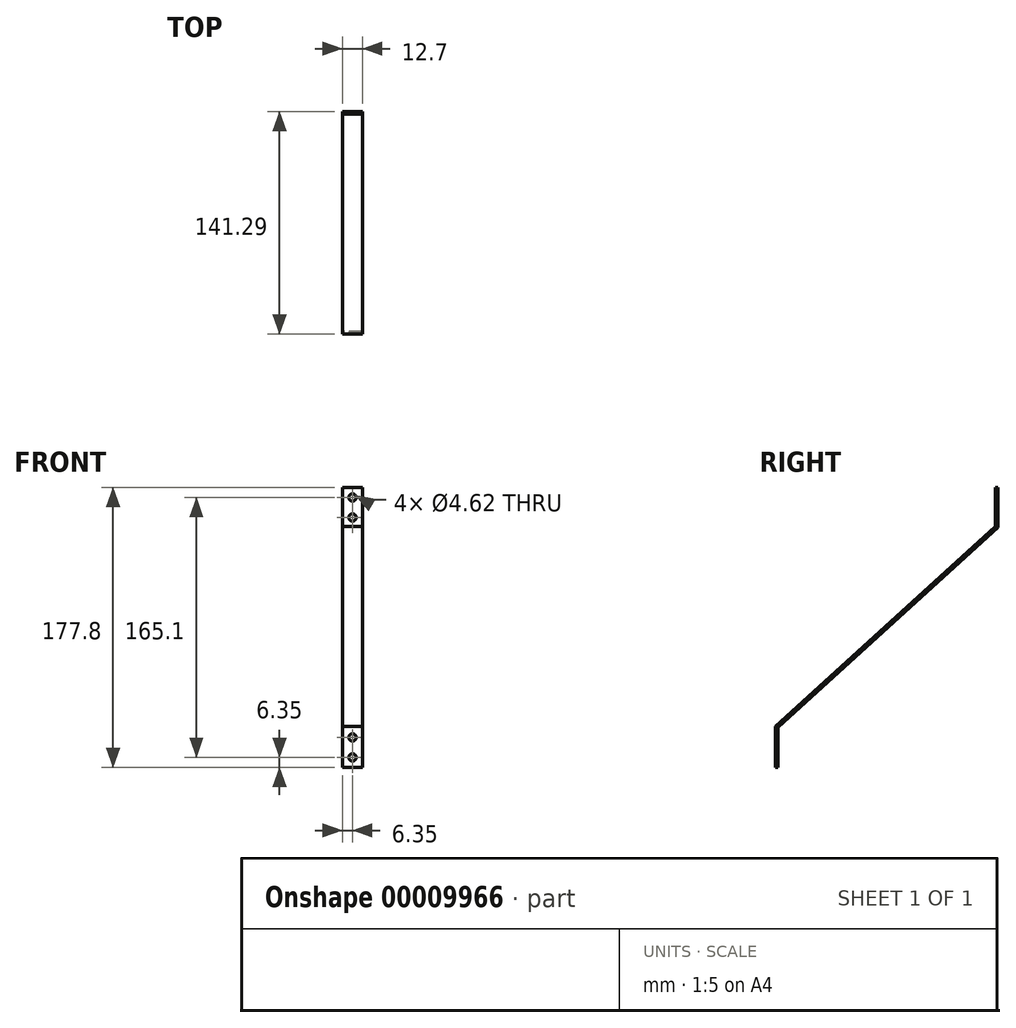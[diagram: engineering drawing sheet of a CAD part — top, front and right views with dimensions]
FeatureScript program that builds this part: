
annotation { "Feature Type Name" : "Feature", "Feature Type Description" : "" }
export const myFeature = defineFeature(function(context is Context, id is Id, definition is map)
    precondition{}
    {
        {
            var Q0;
            Q0=qCreatedBy(makeId("Right.planeOp"),FACE);
            var sketch = newSketch(context, id + "F0", { "sketchPlane" : qUnion([Q0])});
            skLineSegment(sketch, "E0", {"start": v(0, 0) * mm, "end": v(0, 25.4) * mm});
            skLineSegment(sketch, "E1", {"start": v(139.7, 152.4) * mm, "end": v(0, 25.4) * mm});
            skLineSegment(sketch, "E2", {"start": v(139.7, 152.4) * mm, "end": v(139.7, 177.8) * mm});
            skLineSegment(sketch, "E3", {"start": v(139.7, 177.8) * mm, "end": v(138.11, 177.8) * mm});
            skLineSegment(sketch, "E4", {"start": v(138.11, 177.8) * mm, "end": v(138.11, 153.1) * mm});
            skLineSegment(sketch, "E5", {"start": v(-1.59, 26.1) * mm, "end": v(138.11, 153.1) * mm});
            skLineSegment(sketch, "E6", {"start": v(-1.59, 26.1) * mm, "end": v(-1.59, 0) * mm});
            skLineSegment(sketch, "E7", {"start": v(-1.59, 0) * mm, "end": v(0, 0) * mm});
            skSolve(sketch);
        }
        {
            var Q0;
            Q0=makeQuery(id+"F0.imprint","IMPRINT",FACE,{"disambiguationData":[TD([[makeQuery(id+"F0.imprint","IMPRINT",EDGE,{"derivedFrom":sQuery(id+"F0.wireOp",EDGE,"E0")}),1.0]])]});
            extrude(context, id + "F1", {"entities" : qUnion([Q0]), "depth" : 12.7 * mm});
        }
        {
            var Q0;
            Q0=makeQuery(id+"F1.opExtrude","SWEPT_FACE",FACE,{"disambiguationData":[OSD([sQuery(id+"F0.wireOp",EDGE,"E4")])]});
            var sketch = newSketch(context, id + "F2", { "sketchPlane" : qUnion([Q0])});
            skCircle(sketch, "E8", {"center": v(6.35, 171.45) * mm, "radius": 2.31 * mm});
            skCircle(sketch, "E9", {"center": v(6.35, 158.75) * mm, "radius": 2.31 * mm});
            skPoint(sketch, "E10", {"position": v(6.35, 177.8) * mm});
            skSolve(sketch);
        }
        {
            var Q0;
            Q0=makeQuery(id+"F2.imprint","IMPRINT",FACE,{"disambiguationData":[TD([[makeQuery(id+"F2.imprint","IMPRINT",EDGE,{"derivedFrom":sQuery(id+"F2.wireOp",EDGE,"E8")}),1.0]])]});
            var Q1;
            Q1=makeQuery(id+"F2.imprint","IMPRINT",FACE,{"disambiguationData":[TD([[makeQuery(id+"F2.imprint","IMPRINT",EDGE,{"derivedFrom":sQuery(id+"F2.wireOp",EDGE,"E9")}),1.0]])]});
            extrude(context, id + "F3", {"entities" : qUnion([Q0, Q1]), "operationType" : NewBodyOperationType.REMOVE, "endBound" : BoundingType.THROUGH_ALL, "oppositeDirection" : true, "depth" : 25.4 * mm});
        }
        {
            var Q0;
            Q0=makeQuery(id+"F1.opExtrude","SWEPT_FACE",FACE,{"disambiguationData":[OSD([sQuery(id+"F0.wireOp",EDGE,"E6")])]});
            var sketch = newSketch(context, id + "F4", { "sketchPlane" : qUnion([Q0])});
            skCircle(sketch, "E11", {"center": v(6.35, 6.35) * mm, "radius": 2.31 * mm});
            skCircle(sketch, "E12", {"center": v(6.35, 19.05) * mm, "radius": 2.31 * mm});
            skPoint(sketch, "E13", {"position": v(6.35, 0) * mm});
            skSolve(sketch);
        }
        {
            var Q0;
            Q0=makeQuery(id+"F4.imprint","IMPRINT",FACE,{"disambiguationData":[TD([[makeQuery(id+"F4.imprint","IMPRINT",EDGE,{"derivedFrom":sQuery(id+"F4.wireOp",EDGE,"E11")}),1.0]])]});
            var Q1;
            Q1=makeQuery(id+"F4.imprint","IMPRINT",FACE,{"disambiguationData":[TD([[makeQuery(id+"F4.imprint","IMPRINT",EDGE,{"derivedFrom":sQuery(id+"F4.wireOp",EDGE,"E12")}),1.0]])]});
            extrude(context, id + "F5", {"entities" : qUnion([Q0, Q1]), "operationType" : NewBodyOperationType.REMOVE, "endBound" : BoundingType.THROUGH_ALL, "oppositeDirection" : true, "depth" : 25.4 * mm});
        }
    });
